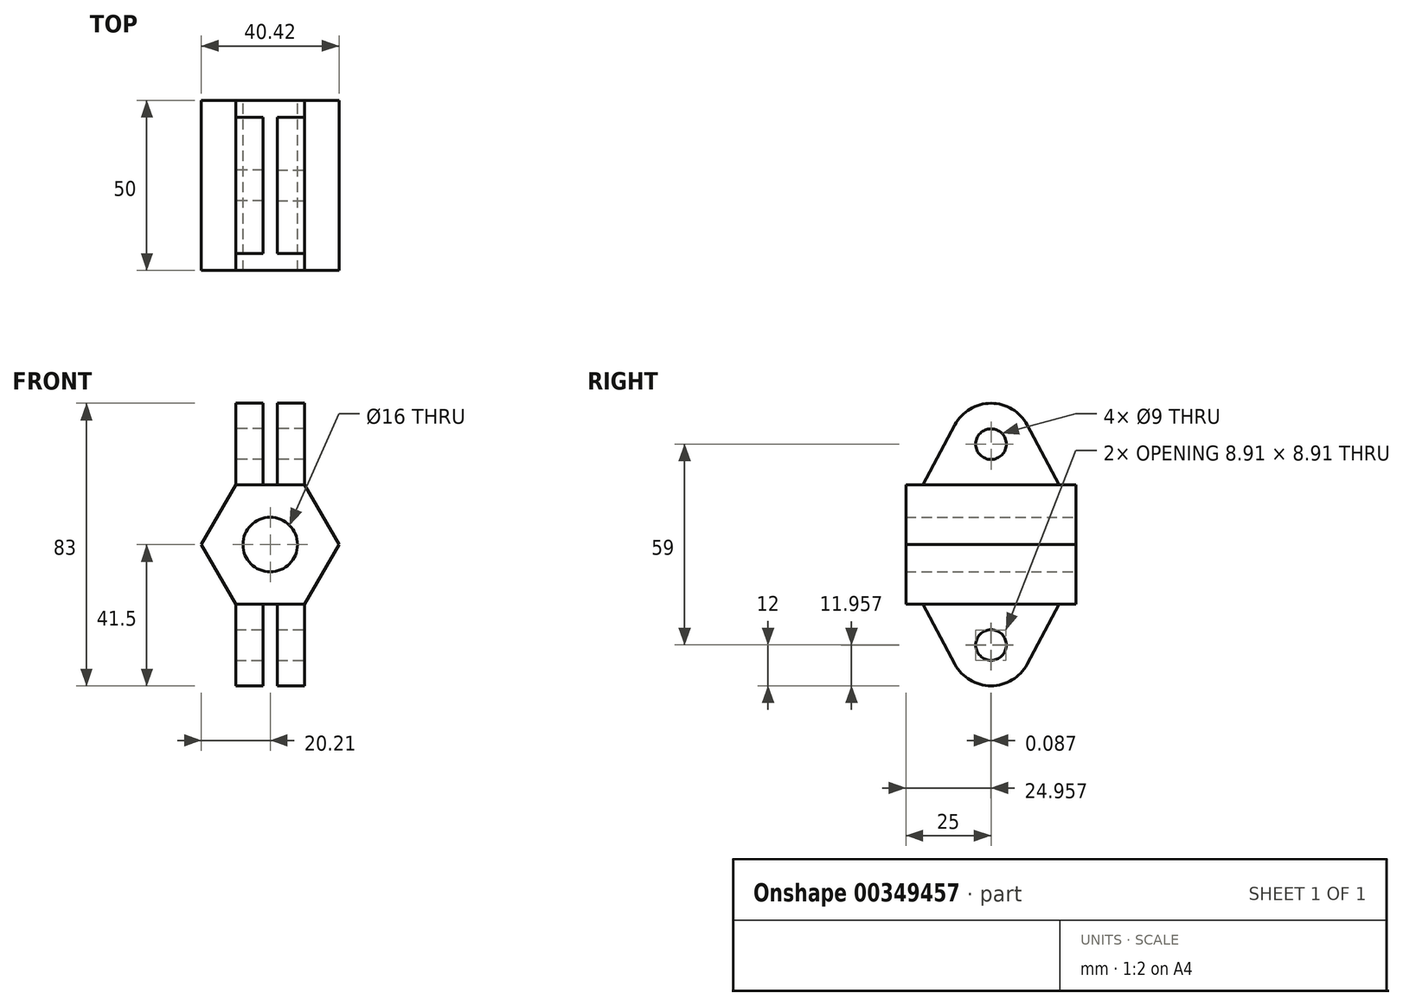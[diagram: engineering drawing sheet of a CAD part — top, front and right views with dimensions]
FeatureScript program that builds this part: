
annotation { "Feature Type Name" : "Feature", "Feature Type Description" : "" }
export const myFeature = defineFeature(function(context is Context, id is Id, definition is map)
    precondition{}
    {
        {
            var Q0;
            Q0=qCreatedBy(makeId("Front.planeOp"),FACE);
            var sketch = newSketch(context, id + "F0", { "sketchPlane" : qUnion([Q0])});
            skCircle(sketch, "E0", {"center": v(0, 0) * mm, "radius": 8 * mm});
            skCircle(sketch, "E1.cCircle", {"center": v(0, 0) * mm, "radius": 17.5 * mm, "construction": true});
            skLineSegment(sketch, "E1.0", {"start": v(-10.1, 17.5) * mm, "end": v(10.1, 17.5) * mm});
            skLineSegment(sketch, "E1.1", {"start": v(10.1, 17.5) * mm, "end": v(20.2, 0) * mm});
            skLineSegment(sketch, "E1.2", {"start": v(20.2, 0) * mm, "end": v(10.1, -17.5) * mm});
            skLineSegment(sketch, "E1.3", {"start": v(10.1, -17.5) * mm, "end": v(-10.1, -17.5) * mm});
            skLineSegment(sketch, "E1.4", {"start": v(-10.1, -17.5) * mm, "end": v(-20.2, 0) * mm});
            skLineSegment(sketch, "E1.5", {"start": v(-20.2, 0) * mm, "end": v(-10.1, 17.5) * mm});
            skPoint(sketch, "E1.0.midPoint", {"position": v(0, 17.5) * mm});
            skSolve(sketch);
        }
        {
            var Q0;
            Q0=qSketchRegion(id+"F0",true);
            extrude(context, id + "F1", {"entities" : qUnion([Q0]), "endBound" : BoundingType.SYMMETRIC, "depth" : 50 * mm});
        }
        {
            var Q0;
            Q0=makeQuery(id+"F1.opExtrude","SWEPT_FACE",FACE,{"disambiguationData":[OSD([sQuery(id+"F0.wireOp",EDGE,"E1.0")])]});
            var sketch = newSketch(context, id + "F2", { "sketchPlane" : qUnion([Q0])});
            skLineSegment(sketch, "E2.bottom", {"start": v(10.1, 20) * mm, "end": v(-10.1, 20) * mm});
            skLineSegment(sketch, "E2.top", {"start": v(10.1, -20) * mm, "end": v(-10.1, -20) * mm});
            skLineSegment(sketch, "E2.left", {"start": v(10.1, 20) * mm, "end": v(10.1, -20) * mm});
            skLineSegment(sketch, "E2.right", {"start": v(-10.1, 20) * mm, "end": v(-10.1, -20) * mm});
            skSolve(sketch);
        }
        {
            var Q0;
            Q0=qSketchRegion(id+"F2",true);
            extrude(context, id + "F3", {"entities" : qUnion([Q0]), "operationType" : NewBodyOperationType.ADD, "depth" : 24 * mm});
        }
        {
            var Q0;
            Q0=makeQuery(id+"F3.opExtrude","SWEPT_FACE",FACE,{"disambiguationData":[OSD([sQuery(id+"F2.wireOp",EDGE,"E2.right")])]});
            var sketch = newSketch(context, id + "F4", { "sketchPlane" : qUnion([Q0])});
            skCircle(sketch, "E3", {"center": v(0, 29.5) * mm, "radius": 4.5 * mm});
            skSolve(sketch);
        }
        {
            var Q0;
            Q0=makeQuery(id+"F4.imprint","IMPRINT",FACE,{"disambiguationData":[TD([[makeQuery(id+"F4.imprint","IMPRINT",EDGE,{"derivedFrom":sQuery(id+"F4.wireOp",EDGE,"E3")}),1.0]])]});
            extrude(context, id + "F5", {"entities" : qUnion([Q0]), "operationType" : NewBodyOperationType.REMOVE, "endBound" : BoundingType.THROUGH_ALL, "oppositeDirection" : true, "depth" : 100 * mm});
        }
        {
            var Q0;
            Q0=makeQuery(id+"F3.opExtrude","SWEPT_FACE",FACE,{"disambiguationData":[OSD([sQuery(id+"F2.wireOp",EDGE,"E2.right")])]});
            var sketch = newSketch(context, id + "F6", { "sketchPlane" : qUnion([Q0])});
            skLineSegment(sketch, "E4", {"start": v(0, 17.5) * mm, "end": v(-20, 17.5) * mm});
            skLineSegment(sketch, "E5", {"start": v(-20, 17.5) * mm, "end": v(-10.59, 35.15) * mm});
            skLineSegment(sketch, "E6.MirrorCS", {"start": v(20, 17.5) * mm, "end": v(10.59, 35.15) * mm});
            skLineSegment(sketch, "E7.MirrorCS", {"start": v(0, 17.5) * mm, "end": v(20, 17.5) * mm});
            skArc(sketch, "E8", {"start": v(10.59, 35.15) * mm, "mid": v(0, 41.5) * mm, "end": v(-10.59, 35.15) * mm});
            skSolve(sketch);
        }
        {
            var Q0;
            {var subQ0=sQuery(id+"F6.wireOp",EDGE,"E5");Q0=makeQuery(id+"F6.imprint","IMPRINT",FACE,{"disambiguationData":[TD([[makeQuery(id+"F6.imprint","IMPRINT",EDGE,{"derivedFrom":subQ0}),1.0]])]});}
            var Q1;
            {var subQ0=sQuery(id+"F6.wireOp",EDGE,"E6.MirrorCS");Q1=makeQuery(id+"F6.imprint","IMPRINT",FACE,{"disambiguationData":[TD([[makeQuery(id+"F6.imprint","IMPRINT",EDGE,{"derivedFrom":subQ0}),-1.0]])]});}
            extrude(context, id + "F7", {"entities" : qUnion([Q0, Q1]), "operationType" : NewBodyOperationType.REMOVE, "oppositeDirection" : true, "depth" : 25.4 * mm});
        }
        {
            var Q0;
            {var subQ2=sQuery(id+"F0.wireOp",EDGE,"E1.0");Q0=makeQuery(id+"F3.boolean.opBoolean","SPLIT",FACE,{"disambiguationData":[TD([makeQuery(id+"F3.opExtrude","SWEPT_FACE",FACE,{"disambiguationData":[OSD([sQuery(id+"F2.wireOp",EDGE,"E2.bottom")])]})])],"derivedFrom":makeQuery(id+"F1.opExtrude","SWEPT_FACE",FACE,{"disambiguationData":[OSD([subQ2])]})});}
            var sketch = newSketch(context, id + "F8", { "sketchPlane" : qUnion([Q0])});
            skLineSegment(sketch, "E9.bottom", {"start": v(-2.1, 25) * mm, "end": v(2.1, 25) * mm});
            skLineSegment(sketch, "E9.top", {"start": v(-2.1, -25) * mm, "end": v(2.1, -25) * mm});
            skLineSegment(sketch, "E9.left", {"start": v(-2.1, 25) * mm, "end": v(-2.1, -25) * mm});
            skLineSegment(sketch, "E9.right", {"start": v(2.1, 25) * mm, "end": v(2.1, -25) * mm});
            skSolve(sketch);
        }
        {
            var Q0;
            Q0=qSketchRegion(id+"F8",true);
            extrude(context, id + "F9", {"entities" : qUnion([Q0]), "operationType" : NewBodyOperationType.REMOVE, "depth" : 25.4 * mm});
        }
        {
            var Q0;
            Q0=makeQuery(id+"F1.opExtrude","SWEPT_FACE",FACE,{"disambiguationData":[OSD([sQuery(id+"F0.wireOp",EDGE,"E1.3")])]});
            var sketch = newSketch(context, id + "F10", { "sketchPlane" : qUnion([Q0])});
            skLineSegment(sketch, "E10.bottom", {"start": v(-10.1, -20) * mm, "end": v(10.1, -20) * mm});
            skLineSegment(sketch, "E10.top", {"start": v(-10.1, 20) * mm, "end": v(10.1, 20) * mm});
            skLineSegment(sketch, "E10.left", {"start": v(-10.1, -20) * mm, "end": v(-10.1, 20) * mm});
            skLineSegment(sketch, "E10.right", {"start": v(10.1, -20) * mm, "end": v(10.1, 20) * mm});
            skSolve(sketch);
        }
        {
            var Q0;
            Q0=qSketchRegion(id+"F10",true);
            extrude(context, id + "F11", {"entities" : qUnion([Q0]), "operationType" : NewBodyOperationType.ADD, "depth" : 24 * mm});
        }
        {
            var Q0;
            Q0=makeQuery(id+"F11.opExtrude","SWEPT_FACE",FACE,{"disambiguationData":[OSD([sQuery(id+"F10.wireOp",EDGE,"E10.right")])]});
            var sketch = newSketch(context, id + "F12", { "sketchPlane" : qUnion([Q0])});
            skCircle(sketch, "E11", {"center": v(0, -29.5) * mm, "radius": 4.5 * mm});
            skPoint(sketch, "E11.centerSnap0", {"position": v(0, -17.5) * mm});
            skSolve(sketch);
        }
        {
            var Q0;
            Q0=qSketchRegion(id+"F12",true);
            extrude(context, id + "F13", {"entities" : qUnion([Q0]), "operationType" : NewBodyOperationType.REMOVE, "oppositeDirection" : true, "depth" : 25.4 * mm});
        }
        {
            var Q0;
            Q0=makeQuery(id+"F11.opExtrude","SWEPT_FACE",FACE,{"disambiguationData":[OSD([sQuery(id+"F10.wireOp",EDGE,"E10.right")])]});
            var sketch = newSketch(context, id + "F14", { "sketchPlane" : qUnion([Q0])});
            skLineSegment(sketch, "E12", {"start": v(0, -17.5) * mm, "end": v(20, -17.5) * mm});
            skLineSegment(sketch, "E13", {"start": v(20, -17.5) * mm, "end": v(10.59, -35.15) * mm});
            skLineSegment(sketch, "E14.MirrorCS", {"start": v(-20, -17.5) * mm, "end": v(-10.59, -35.15) * mm});
            skLineSegment(sketch, "E15.MirrorCS", {"start": v(0, -17.5) * mm, "end": v(-20, -17.5) * mm});
            skArc(sketch, "E16", {"start": v(-10.59, -35.15) * mm, "mid": v(0, -41.5) * mm, "end": v(10.59, -35.15) * mm});
            skSolve(sketch);
        }
        {
            var Q0;
            {var subQ0=sQuery(id+"F14.wireOp",EDGE,"E13");Q0=makeQuery(id+"F14.imprint","IMPRINT",FACE,{"disambiguationData":[TD([[makeQuery(id+"F14.imprint","IMPRINT",EDGE,{"derivedFrom":subQ0}),1.0]])]});}
            var Q1;
            {var subQ0=sQuery(id+"F14.wireOp",EDGE,"E14.MirrorCS");Q1=makeQuery(id+"F14.imprint","IMPRINT",FACE,{"disambiguationData":[TD([[makeQuery(id+"F14.imprint","IMPRINT",EDGE,{"derivedFrom":subQ0}),-1.0]])]});}
            extrude(context, id + "F15", {"entities" : qUnion([Q0, Q1]), "operationType" : NewBodyOperationType.REMOVE, "oppositeDirection" : true, "depth" : 25.4 * mm});
        }
        {
            var Q0;
            {var subQ2=sQuery(id+"F0.wireOp",EDGE,"E1.3");Q0=makeQuery(id+"F11.boolean.opBoolean","SPLIT",FACE,{"disambiguationData":[TD([makeQuery(id+"F11.opExtrude","SWEPT_FACE",FACE,{"disambiguationData":[OSD([sQuery(id+"F10.wireOp",EDGE,"E10.bottom")])]})])],"derivedFrom":makeQuery(id+"F1.opExtrude","SWEPT_FACE",FACE,{"disambiguationData":[OSD([subQ2])]})});}
            var sketch = newSketch(context, id + "F16", { "sketchPlane" : qUnion([Q0])});
            skLineSegment(sketch, "E17.bottom", {"start": v(-2.1, -25) * mm, "end": v(2.1, -25) * mm});
            skLineSegment(sketch, "E17.top", {"start": v(-2.1, 25) * mm, "end": v(2.1, 25) * mm});
            skLineSegment(sketch, "E17.left", {"start": v(-2.1, -25) * mm, "end": v(-2.1, 25) * mm});
            skLineSegment(sketch, "E17.right", {"start": v(2.1, -25) * mm, "end": v(2.1, 25) * mm});
            skSolve(sketch);
        }
        {
            var Q0;
            Q0=qSketchRegion(id+"F16",true);
            extrude(context, id + "F17", {"entities" : qUnion([Q0]), "operationType" : NewBodyOperationType.REMOVE, "depth" : 25.4 * mm});
        }
    });
